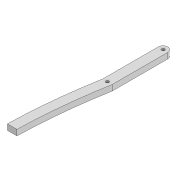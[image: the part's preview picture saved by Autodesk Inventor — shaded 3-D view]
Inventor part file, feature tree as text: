
AUTODESK INVENTOR PART (.ipt)
format: ipt  version: 2022 (Build 260153000, 153)  size: 115,712 bytes
history: native  units: mm
features: extrude x2, sketch x1
ambient origin geometry x8: Origin, YZ Plane, XZ Plane, XY Plane, X Axis, Y Axis, Z Axis, Center Point
bodies: Solid1 (feature_tree)
feature tree (3):
  extrude  "Extrusion1"  Depth=10.0mm
  extrude  "Extrusion2"  Depth=10.0mm
  sketch  "Sketch2"  dims[d0=3.3mm d1=3.3mm d2=10.0mm d3=312.648mm d6=6.0mm d7=0.0mm d10=3.3mm d11=42.6mm d12=3.3mm d13=254.274mm d16=600.0mm d17=600.0mm d18=3.3mm d19=100.0mm d20=10.0mm d21=0.0mm]
